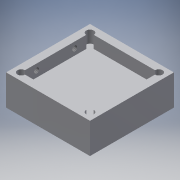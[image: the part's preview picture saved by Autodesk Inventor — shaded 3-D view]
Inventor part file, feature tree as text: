
AUTODESK INVENTOR PART (.ipt)
format: ipt  version: 2016 (Build 200138000, 138)  size: 159,232 bytes
history: native  units: mm
features: sketch x7, hole x4, extrude x3, projected_geometry x3
ambient origin geometry x8: Origin, YZ Plane, XZ Plane, XY Plane, X Axis, Y Axis, Z Axis, Center Point
bodies: Solid1 (feature_tree)
feature tree (17):
  extrude  "Extrusion1"  Depth=55.0mm
  hole  "Hole2"  [1 undecoded]
  extrude  "Extrusion3"  Depth=8.0mm TaperAngle=0.0deg
  hole  "Hole3"  [1 undecoded]
  extrude  "Extrusion4"  Depth=25.0mm
  hole  "Hole5"  [1 undecoded]
  hole  "Hole6"  [1 undecoded]
  sketch  "Sketch1"  dims[d0=55.0mm d1=55.0mm]
  sketch  "Sketch4"  dims[d2=20.0mm d3=0.0mm d15=45.1mm]
  sketch  "Sketch5"  dims[d16=45.1mm]
  sketch  "Sketch6"  dims[d17=5.0mm d18=6.0mm d19=4.0mm d20=2.0mm d21=90.0deg d22=8.0mm d23=0.0mm d24=8.0mm d25=0.0mm]
  projected_geometry  "Projected Loop1"
  sketch  "Sketch8"  dims[d26=15.0mm d27=15.0mm]
  projected_geometry  "Projected Loop2"
  sketch  "Sketch9"  dims[d28=3.242mm d29=6.0mm d30=4.0mm d31=2.0mm d32=90.0deg d33=8.0mm d34=20.594885mm d44=25.0mm]
  projected_geometry  "Projected Loop3"
  sketch  "Sketch10"  dims[d45=25.0mm d46=6.0mm d47=0.0mm d48=3.0mm d49=6.0mm d50=4.0mm d51=2.0mm d52=90.0deg d53=6.0mm d54=0.0mm d55=3.242mm d56=8.0mm d57=4.0mm d58=2.0mm d59=90.0deg d60=4.0mm d61=20.594885mm]
note: 4 required parameter values undecoded (feature->parameter linkage not recoverable at this tier; creation-order binding heuristic only, values carry confidence <= 0.55)
